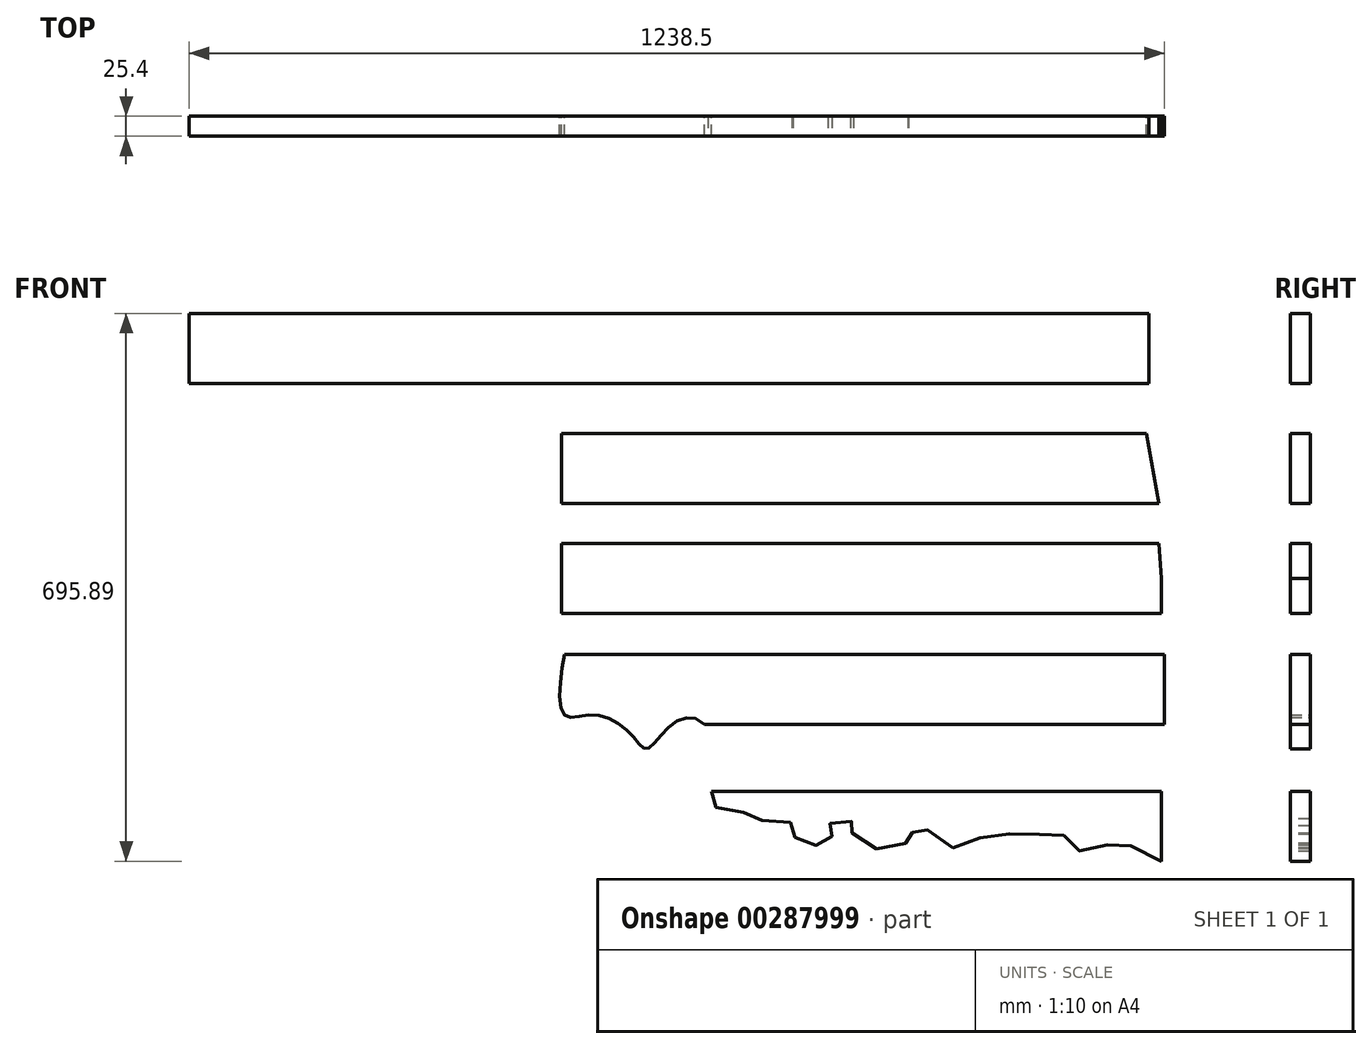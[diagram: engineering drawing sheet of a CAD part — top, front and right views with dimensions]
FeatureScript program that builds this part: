
annotation { "Feature Type Name" : "Feature", "Feature Type Description" : "" }
export const myFeature = defineFeature(function(context is Context, id is Id, definition is map)
    precondition{}
    {
        {
            var Q0;
            Q0=qCreatedBy(makeId("Front.planeOp"),FACE);
            var sketch = newSketch(context, id + "F0", { "sketchPlane" : qUnion([Q0])});
            skLineSegment(sketch, "E0.bottom", {"start": v(0, 0) * mm, "end": v(1219.2, 0) * mm});
            skLineSegment(sketch, "E0.top", {"start": v(0, 88.9) * mm, "end": v(1219.2, 88.9) * mm});
            skLineSegment(sketch, "E0.left", {"start": v(0, 0) * mm, "end": v(0, 88.9) * mm});
            skLineSegment(sketch, "E0.right", {"start": v(1219.2, 0) * mm, "end": v(1219.2, 88.9) * mm});
            skSolve(sketch);
        }
        {
            var Q0;
            Q0=makeQuery(id+"F0.imprint","IMPRINT",FACE,{"disambiguationData":[TD([[makeQuery(id+"F0.imprint","IMPRINT",EDGE,{"derivedFrom":sQuery(id+"F0.wireOp",EDGE,"E0.bottom")}),1.0]])]});
            extrude(context, id + "F1", {"entities" : qUnion([Q0]), "depth" : 25.4 * mm});
        }
        {
            var Q0;
            Q0=qCreatedBy(makeId("Front.planeOp"),FACE);
            var sketch = newSketch(context, id + "F2", { "sketchPlane" : qUnion([Q0])});
            skLineSegment(sketch, "E1.bottom", {"start": v(1215.64, -63.5) * mm, "end": v(472.69, -63.5) * mm});
            skLineSegment(sketch, "E1.top", {"start": v(1215.64, -152.4) * mm, "end": v(472.69, -152.4) * mm});
            skLineSegment(sketch, "E1.right", {"start": v(472.69, -63.5) * mm, "end": v(472.69, -152.4) * mm});
            skLineSegment(sketch, "E2", {"start": v(1215.64, -152.4) * mm, "end": v(1231.51, -152.4) * mm});
            skLineSegment(sketch, "E3", {"start": v(1231.51, -152.4) * mm, "end": v(1215.64, -63.5) * mm});
            skSolve(sketch);
        }
        {
            var Q0;
            Q0=makeQuery(id+"F2.imprint","IMPRINT",FACE,{"disambiguationData":[TD([[makeQuery(id+"F2.imprint","IMPRINT",EDGE,{"derivedFrom":sQuery(id+"F2.wireOp",EDGE,"E1.bottom")}),1.0]])]});
            extrude(context, id + "F3", {"entities" : qUnion([Q0]), "depth" : 25.4 * mm});
        }
        {
            var Q0;
            Q0=qCreatedBy(makeId("Front.planeOp"),FACE);
            var sketch = newSketch(context, id + "F4", { "sketchPlane" : qUnion([Q0])});
            skLineSegment(sketch, "E4.0", {"start": v(1231.51, -203.2) * mm, "end": v(472.69, -203.2) * mm});
            skLineSegment(sketch, "E5", {"start": v(472.69, -203.2) * mm, "end": v(472.69, -292.1) * mm});
            skLineSegment(sketch, "E6", {"start": v(472.69, -292.1) * mm, "end": v(1234.69, -292.1) * mm});
            skLineSegment(sketch, "E7", {"start": v(1234.69, -292.1) * mm, "end": v(1234.69, -247.65) * mm});
            skPoint(sketch, "E7.endSnap0", {"position": v(472.69, -247.65) * mm});
            skLineSegment(sketch, "E8", {"start": v(1234.69, -247.65) * mm, "end": v(1231.51, -203.2) * mm});
            skSolve(sketch);
        }
        {
            var Q0;
            Q0=makeQuery(id+"F4.imprint","IMPRINT",FACE,{"disambiguationData":[TD([[makeQuery(id+"F4.imprint","IMPRINT",EDGE,{"derivedFrom":sQuery(id+"F4.wireOp",EDGE,"E4.0")}),1.0]])]});
            extrude(context, id + "F5", {"entities" : qUnion([Q0]), "depth" : 25.4 * mm});
        }
        {
            var Q0;
            Q0=qCreatedBy(makeId("Front.planeOp"),FACE);
            var sketch = newSketch(context, id + "F6", { "sketchPlane" : qUnion([Q0])});
            skLineSegment(sketch, "E9", {"start": v(476.5, -293.47) * mm, "end": v(476.5, -344.27) * mm});
            skLineSegment(sketch, "E10", {"start": v(476.5, -344.27) * mm, "end": v(1238.5, -344.27) * mm});
            skLineSegment(sketch, "E11", {"start": v(1238.5, -344.27) * mm, "end": v(1238.5, -433.17) * mm});
            skLineSegment(sketch, "E12", {"start": v(1238.5, -433.17) * mm, "end": v(654.3, -433.17) * mm});
            skFitSpline(sketch, "E13", {"points": [v(476.5, -344.27) * mm, v(476.5, -421.2) * mm, v(512.53, -421.2) * mm, v(560.98, -445.43) * mm, v(581.49, -464.07) * mm, v(611.3, -434.25) * mm, v(654.3, -433.17) * mm], "startDerivative": vector(-68.25, -372.14) * mm, "endDerivative": vector(231.96, -251.8) * mm});
            skSolve(sketch);
        }
        {
            var Q0;
            Q0 = qSketchRegion(id + "F6", true);
            extrude(context, id + "F7", {"entities" : qUnion([Q0]), "depth" : 25.4 * mm});
        }
        {
            var Q0;
            Q0=qCreatedBy(makeId("Front.planeOp"),FACE);
            var sketch = newSketch(context, id + "F8", { "sketchPlane" : qUnion([Q0])});
            skLineSegment(sketch, "E14", {"start": v(1234.73, -518.09) * mm, "end": v(663.23, -518.09) * mm});
            skLineSegment(sketch, "E15", {"start": v(1234.73, -518.09) * mm, "end": v(1234.73, -606.99) * mm});
            skFitSpline(sketch, "E16", {"points": [v(1234.73, -606.99) * mm, v(1189.62, -585.69) * mm, v(1165.24, -586.8) * mm, v(1128.67, -593.44) * mm, v(1113.16, -575.71) * mm, v(1088.78, -572.39) * mm, v(1048.88, -572.39) * mm, v(1007.88, -575.71) * mm, v(971.31, -590.12) * mm, v(936.96, -565.74) * mm, v(933.63, -562.41) * mm, v(913.68, -575.71) * mm, v(913.68, -581.25) * mm, v(901.5, -586.8) * mm, v(854.95, -586.8) * mm, v(840.54, -562.41) * mm, v(843.87, -560.2) * mm, v(835, -553.55) * mm, v(812.84, -560.2) * mm, v(811.73, -563.52) * mm, v(816.16, -575.71) * mm, v(801.76, -585.69) * mm, v(789.57, -585.69) * mm, v(766.3, -572.39) * mm, v(766.3, -560.2) * mm, v(744.13, -555.77) * mm, v(708.67, -551.33) * mm, v(700.91, -542.47) * mm, v(661.02, -535.82) * mm, v(663.23, -518.09) * mm], "startDerivative": vector(-945.69, 518.56) * mm, "endDerivative": vector(323.08, 681.26) * mm});
            skSolve(sketch);
        }
        {
            var Q0;
            Q0=makeQuery(id+"F8.imprint","IMPRINT",FACE,{"disambiguationData":[TD([[makeQuery(id+"F8.imprint","IMPRINT",EDGE,{"derivedFrom":sQuery(id+"F8.wireOp",EDGE,"E14")}),1.0]])]});
            extrude(context, id + "F9", {"entities" : qUnion([Q0]), "depth" : 25.4 * mm});
        }
    });
